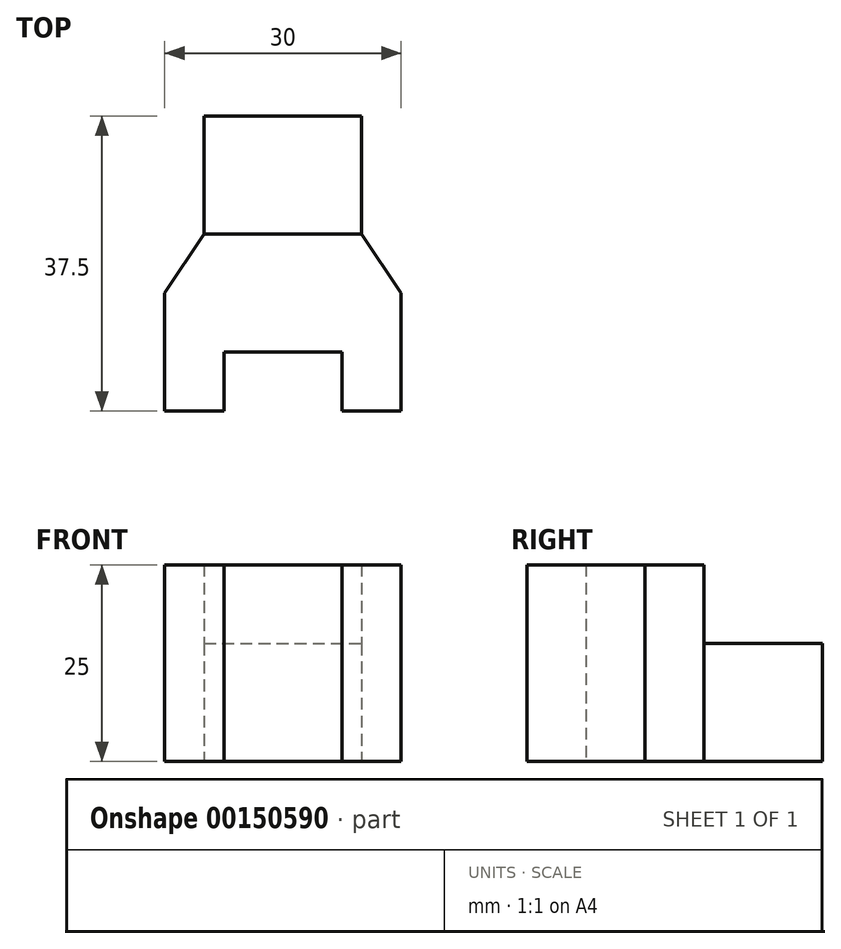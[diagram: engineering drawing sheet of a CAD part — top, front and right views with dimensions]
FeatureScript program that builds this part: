
annotation { "Feature Type Name" : "Feature", "Feature Type Description" : "" }
export const myFeature = defineFeature(function(context is Context, id is Id, definition is map)
    precondition{}
    {
        {
            var Q0;
            Q0=qCreatedBy(makeId("Top.planeOp"),FACE);
            var sketch = newSketch(context, id + "F0", { "sketchPlane" : qUnion([Q0])});
            skLineSegment(sketch, "E0", {"start": v(0, 0) * mm, "end": v(0, -15) * mm});
            skLineSegment(sketch, "E1", {"start": v(0, -15) * mm, "end": v(-5, -22.5) * mm});
            skLineSegment(sketch, "E2", {"start": v(-5, -22.5) * mm, "end": v(-5, -37.5) * mm});
            skLineSegment(sketch, "E3", {"start": v(-5, -37.5) * mm, "end": v(2.5, -37.5) * mm});
            skLineSegment(sketch, "E4", {"start": v(2.5, -37.5) * mm, "end": v(2.5, -30) * mm});
            skLineSegment(sketch, "E5", {"start": v(2.5, -30) * mm, "end": v(17.5, -30) * mm});
            skLineSegment(sketch, "E6", {"start": v(17.5, -30) * mm, "end": v(17.5, -37.5) * mm});
            skLineSegment(sketch, "E7", {"start": v(17.5, -37.5) * mm, "end": v(25, -37.5) * mm});
            skLineSegment(sketch, "E8", {"start": v(25, -37.5) * mm, "end": v(25, -22.5) * mm});
            skLineSegment(sketch, "E9", {"start": v(25, -22.5) * mm, "end": v(20, -15) * mm});
            skLineSegment(sketch, "E10", {"start": v(20, -15) * mm, "end": v(20, 0) * mm});
            skLineSegment(sketch, "E11", {"start": v(0, 0) * mm, "end": v(20, 0) * mm});
            skLineSegment(sketch, "E12", {"start": v(0, -15) * mm, "end": v(20, -15) * mm});
            skSolve(sketch);
        }
        {
            var Q0;
            Q0=makeQuery(id+"F0.imprint","IMPRINT",FACE,{"disambiguationData":[TD([[makeQuery(id+"F0.imprint","IMPRINT",EDGE,{"derivedFrom":sQuery(id+"F0.wireOp",EDGE,"E0")}),1.0]])]});
            extrude(context, id + "F1", {"entities" : qUnion([Q0]), "depth" : 15 * mm});
        }
        {
            var Q0;
            Q0=makeQuery(id+"F0.imprint","IMPRINT",FACE,{"disambiguationData":[TD([[makeQuery(id+"F0.imprint","IMPRINT",EDGE,{"derivedFrom":sQuery(id+"F0.wireOp",EDGE,"E1")}),1.0]])]});
            extrude(context, id + "F2", {"entities" : qUnion([Q0]), "operationType" : NewBodyOperationType.ADD, "depth" : 25 * mm});
        }
    });
